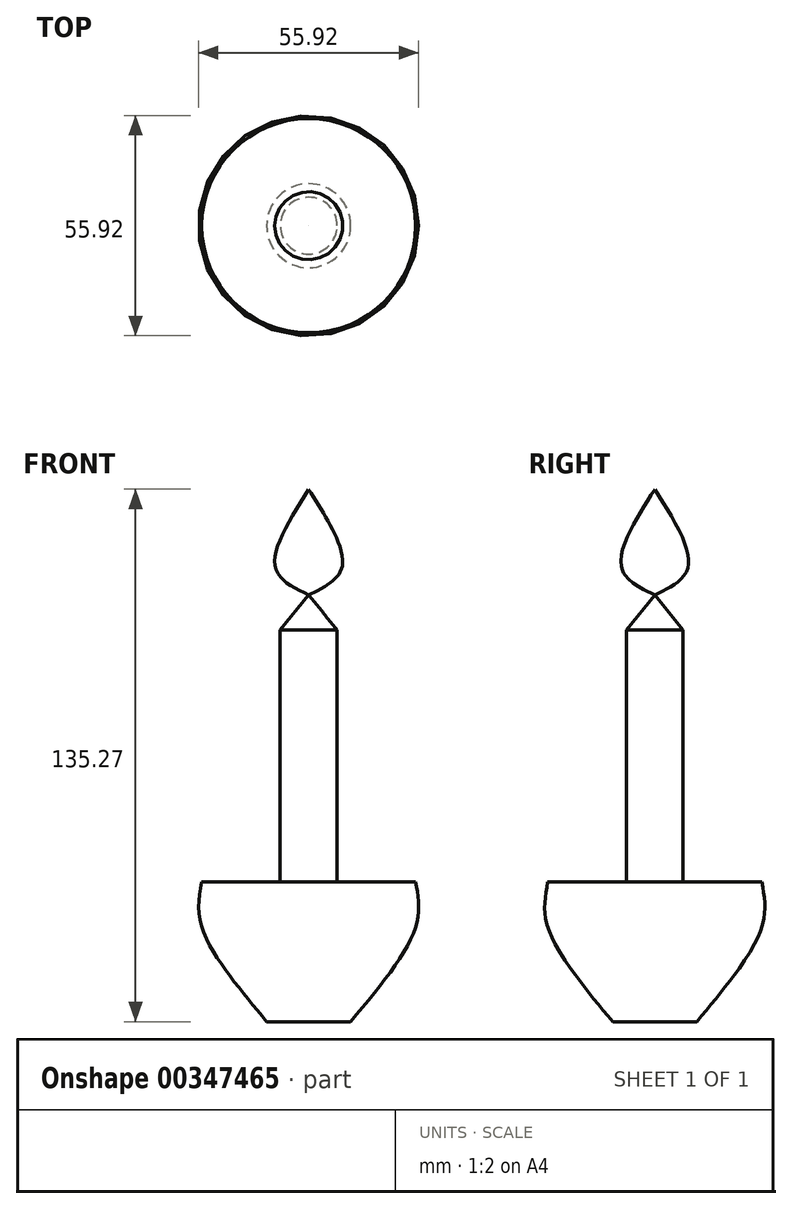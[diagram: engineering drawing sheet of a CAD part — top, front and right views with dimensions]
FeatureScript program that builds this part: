
annotation { "Feature Type Name" : "Feature", "Feature Type Description" : "" }
export const myFeature = defineFeature(function(context is Context, id is Id, definition is map)
    precondition{}
    {
        {
            var Q0;
            Q0=qCreatedBy(makeId("Front.planeOp"),FACE);
            var sketch = newSketch(context, id + "F0", { "sketchPlane" : qUnion([Q0])});
            skLineSegment(sketch, "E0", {"start": v(0, 43.03) * mm, "end": v(-7.23, 34.08) * mm});
            skLineSegment(sketch, "E1", {"start": v(-7.23, 34.08) * mm, "end": v(-7.23, -29.95) * mm});
            skLineSegment(sketch, "E2", {"start": v(-7.23, -29.95) * mm, "end": v(-27.2, -29.95) * mm});
            skFitSpline(sketch, "E3", {"points": [v(-27.2, -29.95) * mm, v(-27.2, -41.31) * mm, v(-10.67, -65.41) * mm], "startDerivative": vector(-5.15, -27.75) * mm, "endDerivative": vector(35.1, -42.07) * mm});
            skLineSegment(sketch, "E4", {"start": v(-10.67, -65.41) * mm, "end": v(0, -65.41) * mm});
            skLineSegment(sketch, "E5", {"start": v(0, -65.41) * mm, "end": v(0, 43.03) * mm});
            skLineSegment(sketch, "E6", {"start": v(0, 76.08) * mm, "end": v(0, -81.94) * mm, "construction": true});
            skSolve(sketch);
        }
        {
            var Q0;
            Q0=makeQuery(id+"F0.imprint","IMPRINT",FACE,{"disambiguationData":[TD([[makeQuery(id+"F0.imprint","IMPRINT",EDGE,{"derivedFrom":sQuery(id+"F0.wireOp",EDGE,"E0")}),1.0]])]});
            var Q1;
            Q1=sQuery(id+"F0.wireOp",EDGE,"E6");
            revolve(context, id + "F1", {"entities" : qUnion([Q0]), "axis" : qUnion([Q1]), "revolveType" : RevolveType.FULL});
        }
        {
            var Q0;
            Q0=qCreatedBy(makeId("Front.planeOp"),FACE);
            var sketch = newSketch(context, id + "F2", { "sketchPlane" : qUnion([Q0])});
            skPoint(sketch, "E7.0.internal.orphan", {"position": v(0, 43.02) * mm});
            skPoint(sketch, "E7.3.internal.orphan", {"position": v(0, 63.98) * mm});
            skFitSpline(sketch, "E8", {"points": [v(0, 43.02) * mm, v(-8.46, 50) * mm, v(0, 69.86) * mm], "startDerivative": vector(-27.56, 13.2) * mm, "endDerivative": vector(24.64, 39.04) * mm});
            skLineSegment(sketch, "E9", {"start": v(0, 69.86) * mm, "end": v(0, 43.02) * mm});
            skSolve(sketch);
        }
        {
            var Q0;
            Q0=makeQuery(id+"F2.imprint","IMPRINT",FACE,{"disambiguationData":[TD([[makeQuery(id+"F2.imprint","IMPRINT",EDGE,{"derivedFrom":sQuery(id+"F2.wireOp",EDGE,"E8")}),-1.0]])]});
            var Q1;
            Q1=sQuery(id+"F2.wireOp",EDGE,"E9");
            revolve(context, id + "F3", {"operationType" : NewBodyOperationType.ADD, "entities" : qUnion([Q0]), "axis" : qUnion([Q1]), "revolveType" : RevolveType.FULL});
        }
    });
